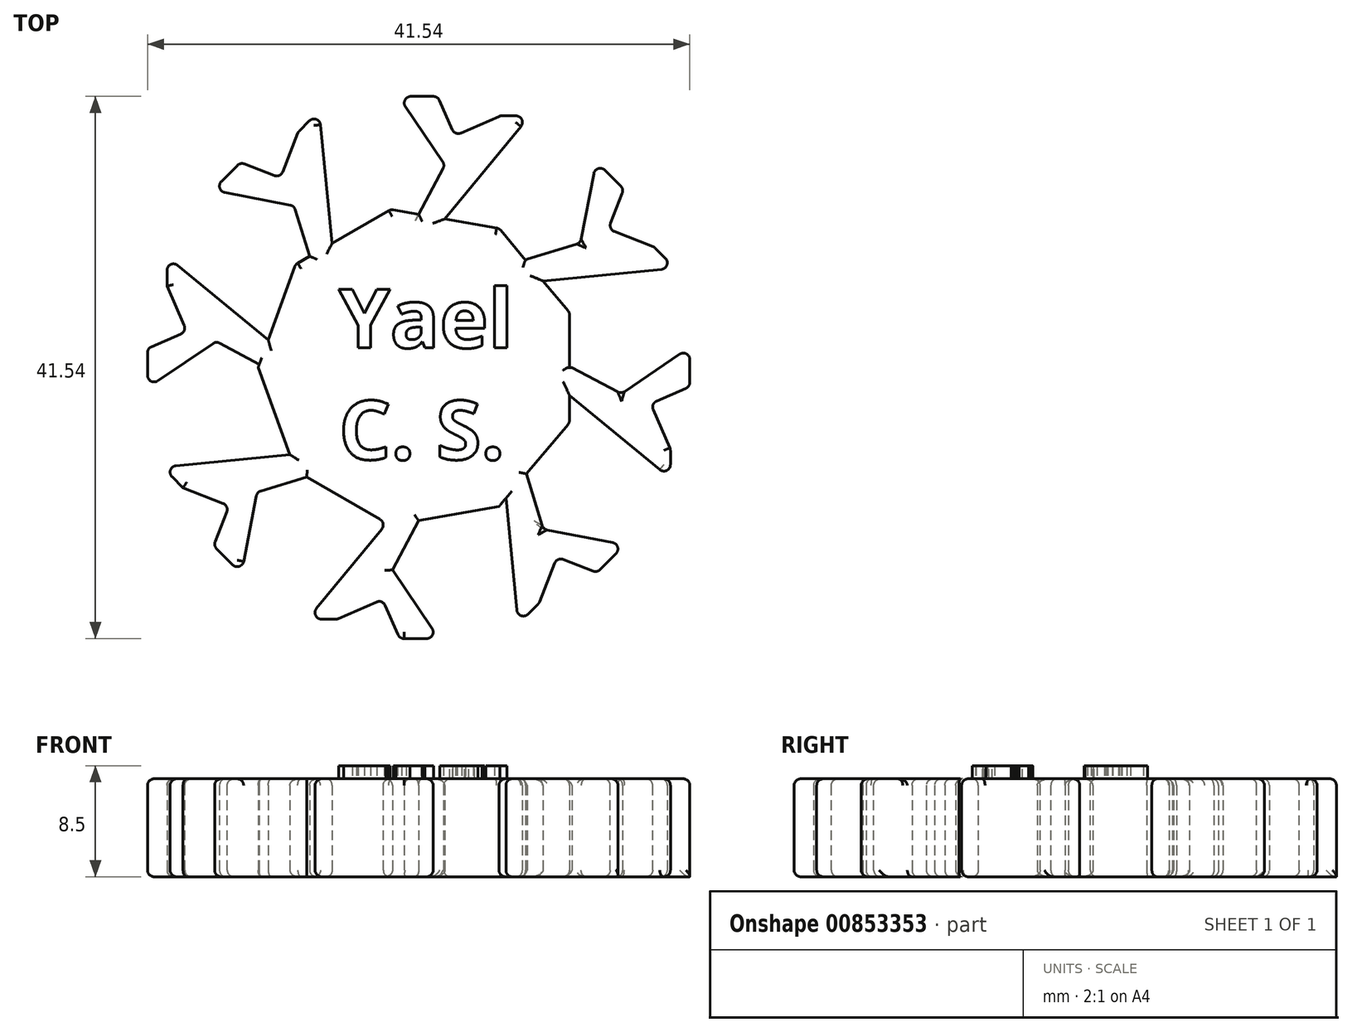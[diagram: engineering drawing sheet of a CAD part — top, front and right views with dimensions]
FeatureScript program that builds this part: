
annotation { "Feature Type Name" : "Feature", "Feature Type Description" : "" }
export const myFeature = defineFeature(function(context is Context, id is Id, definition is map)
    precondition{}
    {
        {
            var Q0;
            Q0=qCreatedBy(makeId("Top.planeOp"),FACE);
            var sketch = newSketch(context, id + "F0", { "sketchPlane" : qUnion([Q0])});
            skLineSegment(sketch, "E0.cCircle", {"start": v(11.56, 0) * mm, "end": v(11.56, 0) * mm});
            skLineSegment(sketch, "E0.0", {"start": v(11.56, 4.2) * mm, "end": v(11.56, 0) * mm});
            skLineSegment(sketch, "E0.1", {"start": v(11.56, -4.2) * mm, "end": v(8.25, -8.15) * mm});
            skLineSegment(sketch, "E0.2", {"start": v(6.15, -10.65) * mm, "end": v(0, -11.74) * mm});
            skLineSegment(sketch, "E0.3", {"start": v(-2.46, -11.93) * mm, "end": v(-8.6, -8.39) * mm});
            skLineSegment(sketch, "E0.4", {"start": v(-9.87, -6.67) * mm, "end": v(-12.3, 0) * mm});
            skLineSegment(sketch, "E0.5", {"start": v(-12.3, 0) * mm, "end": v(-12.21, 0.25) * mm});
            skLineSegment(sketch, "E0.6", {"start": v(-9.42, 7.9) * mm, "end": v(-8.37, 8.52) * mm});
            skLineSegment(sketch, "E0.7", {"start": v(-2.14, 12.12) * mm, "end": v(0, 11.74) * mm});
            skLineSegment(sketch, "E0.8", {"start": v(6.15, 10.65) * mm, "end": v(8.2, 8.21) * mm});
            skPoint(sketch, "E0.0.midPoint", {"position": v(11.56, 0) * mm});
            skLineSegment(sketch, "E1", {"start": v(-1.55, 20.77) * mm, "end": v(1.46, 20.77) * mm});
            skLineSegment(sketch, "E2", {"start": v(1.46, 20.77) * mm, "end": v(2.77, 17.77) * mm});
            skLineSegment(sketch, "E3", {"start": v(2.77, 17.77) * mm, "end": v(6.25, 19.29) * mm});
            skLineSegment(sketch, "E4", {"start": v(6.25, 19.29) * mm, "end": v(8.5, 19.29) * mm});
            skLineSegment(sketch, "E5", {"start": v(8.5, 19.29) * mm, "end": v(2, 11.38) * mm});
            skLineSegment(sketch, "E6", {"start": v(0, 11.74) * mm, "end": v(2, 15.51) * mm});
            skLineSegment(sketch, "E7", {"start": v(2, 15.51) * mm, "end": v(-1.55, 20.77) * mm});
            skLineSegment(sketch, "E8.1.0", {"start": v(-9.55, 12.39) * mm, "end": v(-15.78, 13.6) * mm});
            skLineSegment(sketch, "E8.1.1", {"start": v(-15.78, 13.6) * mm, "end": v(-13.66, 15.72) * mm});
            skLineSegment(sketch, "E8.1.2", {"start": v(-13.66, 15.72) * mm, "end": v(-10.6, 14.52) * mm});
            skLineSegment(sketch, "E8.1.3", {"start": v(-10.6, 14.52) * mm, "end": v(-9.22, 18.05) * mm});
            skLineSegment(sketch, "E8.1.4", {"start": v(-9.22, 18.05) * mm, "end": v(-7.63, 19.65) * mm});
            skLineSegment(sketch, "E8.1.5", {"start": v(-7.63, 19.65) * mm, "end": v(-6.63, 9.47) * mm});
            skLineSegment(sketch, "E8.1.6", {"start": v(-8.37, 8.52) * mm, "end": v(-9.55, 12.39) * mm});
            skLineSegment(sketch, "E8.2.0", {"start": v(-15.51, 2) * mm, "end": v(-20.77, -1.55) * mm});
            skLineSegment(sketch, "E8.2.1", {"start": v(-20.77, -1.55) * mm, "end": v(-20.77, 1.46) * mm});
            skLineSegment(sketch, "E8.2.2", {"start": v(-20.77, 1.46) * mm, "end": v(-17.77, 2.77) * mm});
            skLineSegment(sketch, "E8.2.3", {"start": v(-17.77, 2.77) * mm, "end": v(-19.29, 6.25) * mm});
            skLineSegment(sketch, "E8.2.4", {"start": v(-19.29, 6.25) * mm, "end": v(-19.29, 8.5) * mm});
            skLineSegment(sketch, "E8.2.5", {"start": v(-19.29, 8.5) * mm, "end": v(-11.38, 2) * mm});
            skLineSegment(sketch, "E8.2.6", {"start": v(-12.21, 0.25) * mm, "end": v(-15.51, 2) * mm});
            skLineSegment(sketch, "E8.3.0", {"start": v(-12.39, -9.55) * mm, "end": v(-13.6, -15.78) * mm});
            skLineSegment(sketch, "E8.3.1", {"start": v(-13.6, -15.78) * mm, "end": v(-15.72, -13.66) * mm});
            skLineSegment(sketch, "E8.3.2", {"start": v(-15.72, -13.66) * mm, "end": v(-14.52, -10.6) * mm});
            skLineSegment(sketch, "E8.3.3", {"start": v(-14.52, -10.6) * mm, "end": v(-18.05, -9.22) * mm});
            skLineSegment(sketch, "E8.3.4", {"start": v(-18.05, -9.22) * mm, "end": v(-19.65, -7.63) * mm});
            skLineSegment(sketch, "E8.3.5", {"start": v(-19.65, -7.63) * mm, "end": v(-9.47, -6.63) * mm});
            skLineSegment(sketch, "E8.3.6", {"start": v(-8.3, -8.3) * mm, "end": v(-12.39, -9.55) * mm});
            skLineSegment(sketch, "E8.4.0", {"start": v(-2, -15.51) * mm, "end": v(1.55, -20.77) * mm});
            skLineSegment(sketch, "E8.4.1", {"start": v(1.55, -20.77) * mm, "end": v(-1.46, -20.77) * mm});
            skLineSegment(sketch, "E8.4.2", {"start": v(-1.46, -20.77) * mm, "end": v(-2.77, -17.77) * mm});
            skLineSegment(sketch, "E8.4.3", {"start": v(-2.77, -17.77) * mm, "end": v(-6.25, -19.29) * mm});
            skLineSegment(sketch, "E8.4.4", {"start": v(-6.25, -19.29) * mm, "end": v(-8.5, -19.29) * mm});
            skLineSegment(sketch, "E8.4.5", {"start": v(-8.5, -19.29) * mm, "end": v(-2.46, -11.93) * mm});
            skLineSegment(sketch, "E8.4.6", {"start": v(0, -11.74) * mm, "end": v(-2, -15.51) * mm});
            skLineSegment(sketch, "E8.5.0", {"start": v(9.55, -12.39) * mm, "end": v(15.78, -13.6) * mm});
            skLineSegment(sketch, "E8.5.1", {"start": v(15.78, -13.6) * mm, "end": v(13.66, -15.72) * mm});
            skLineSegment(sketch, "E8.5.2", {"start": v(13.66, -15.72) * mm, "end": v(10.6, -14.52) * mm});
            skLineSegment(sketch, "E8.5.3", {"start": v(10.6, -14.52) * mm, "end": v(9.22, -18.05) * mm});
            skLineSegment(sketch, "E8.5.4", {"start": v(9.22, -18.05) * mm, "end": v(7.63, -19.65) * mm});
            skLineSegment(sketch, "E8.5.5", {"start": v(7.63, -19.65) * mm, "end": v(6.68, -10.02) * mm});
            skLineSegment(sketch, "E8.5.6", {"start": v(8.3, -8.3) * mm, "end": v(9.55, -12.39) * mm});
            skLineSegment(sketch, "E8.6.0", {"start": v(15.51, -2) * mm, "end": v(20.77, 1.55) * mm});
            skLineSegment(sketch, "E8.6.1", {"start": v(20.77, 1.55) * mm, "end": v(20.77, -1.46) * mm});
            skLineSegment(sketch, "E8.6.2", {"start": v(20.77, -1.46) * mm, "end": v(17.77, -2.77) * mm});
            skLineSegment(sketch, "E8.6.3", {"start": v(17.77, -2.77) * mm, "end": v(19.29, -6.25) * mm});
            skLineSegment(sketch, "E8.6.4", {"start": v(19.29, -6.25) * mm, "end": v(19.29, -8.5) * mm});
            skLineSegment(sketch, "E8.6.5", {"start": v(19.29, -8.5) * mm, "end": v(11.38, -2) * mm});
            skLineSegment(sketch, "E8.6.6", {"start": v(11.74, 0) * mm, "end": v(15.51, -2) * mm});
            skLineSegment(sketch, "E8.7.0", {"start": v(12.39, 9.55) * mm, "end": v(13.6, 15.78) * mm});
            skLineSegment(sketch, "E8.7.1", {"start": v(13.6, 15.78) * mm, "end": v(15.72, 13.66) * mm});
            skLineSegment(sketch, "E8.7.2", {"start": v(15.72, 13.66) * mm, "end": v(14.52, 10.6) * mm});
            skLineSegment(sketch, "E8.7.3", {"start": v(14.52, 10.6) * mm, "end": v(18.05, 9.22) * mm});
            skLineSegment(sketch, "E8.7.4", {"start": v(18.05, 9.22) * mm, "end": v(19.65, 7.63) * mm});
            skLineSegment(sketch, "E8.7.5", {"start": v(19.65, 7.63) * mm, "end": v(9.47, 6.63) * mm});
            skLineSegment(sketch, "E8.7.6", {"start": v(8.3, 8.3) * mm, "end": v(12.39, 9.55) * mm});
            skLineSegment(sketch, "E9", {"start": v(8.3, 8.3) * mm, "end": v(8.2, 8.21) * mm});
            skLineSegment(sketch, "E10", {"start": v(11.74, 0) * mm, "end": v(11.56, 0) * mm});
            skLineSegment(sketch, "E11", {"start": v(8.3, -8.3) * mm, "end": v(8.25, -8.15) * mm});
            skPoint(sketch, "E12.orphan", {"position": v(-2.14, -12.12) * mm});
            skLineSegment(sketch, "E13.trimOffspring", {"start": v(6.68, -10.02) * mm, "end": v(6.15, -10.65) * mm});
            skPoint(sketch, "E14.orphan", {"position": v(-9.42, -7.9) * mm});
            skLineSegment(sketch, "E15.trimOffspring", {"start": v(11.56, -2.15) * mm, "end": v(11.56, -4.2) * mm});
            skArc(sketch, "E16.trimOffspring", {"start": v(-5.78, 10.01) * mm, "mid": v(-6.21, 9.75) * mm, "end": v(-6.63, 9.47) * mm, "construction": true});
            skPoint(sketch, "E17.orphan", {"position": v(-2, -11.38) * mm});
            skPoint(sketch, "E18.orphan", {"position": v(6.63, -9.47) * mm});
            skLineSegment(sketch, "E19.trimOffspring", {"start": v(-11.53, 2.13) * mm, "end": v(-9.42, 7.9) * mm});
            skPoint(sketch, "E20.orphan", {"position": v(-11.74, 0) * mm});
            skPoint(sketch, "E21.orphan", {"position": v(-8.3, 8.3) * mm});
            skLineSegment(sketch, "E22.trimOffspring", {"start": v(9.52, 6.64) * mm, "end": v(11.56, 4.2) * mm});
            skLineSegment(sketch, "E23.trimOffspring", {"start": v(2, 11.38) * mm, "end": v(6.15, 10.65) * mm});
            skLineSegment(sketch, "E24.trimOffspring", {"start": v(-6.64, 9.52) * mm, "end": v(-2.14, 12.12) * mm});
            skSolve(sketch);
        }
        {
            var Q0;
            Q0=makeQuery(id+"F0.imprint","IMPRINT",FACE,{"disambiguationData":[TD([[makeQuery(id+"F0.imprint","IMPRINT",EDGE,{"derivedFrom":sQuery(id+"F0.wireOp",EDGE,"E0.0")}),-1.0]])]});
            extrude(context, id + "F1", {"entities" : qUnion([Q0]), "depth" : 7.5 * mm, "offsetDistance" : 25 * mm});
        }
        {
            var Q0;
            Q0=makeQuery(id+"F1.opExtrude","CAP_EDGE",EDGE,{"disambiguationData":[OSD([sQuery(id+"F0.wireOp",EDGE,"E8.1.2")])],"isStart":false});
            var Q1;
            Q1=makeQuery(id+"F1.opExtrude","CAP_EDGE",EDGE,{"disambiguationData":[OSD([sQuery(id+"F0.wireOp",EDGE,"E8.1.1")])],"isStart":false});
            var Q2;
            Q2=makeQuery(id+"F1.opExtrude","CAP_EDGE",EDGE,{"disambiguationData":[OSD([sQuery(id+"F0.wireOp",EDGE,"E8.1.0")])],"isStart":false});
            var Q3;
            Q3=makeQuery(id+"F1.opExtrude","CAP_EDGE",EDGE,{"disambiguationData":[OSD([sQuery(id+"F0.wireOp",EDGE,"E8.1.3")])],"isStart":false});
            var Q4;
            Q4=makeQuery(id+"F1.opExtrude","CAP_EDGE",EDGE,{"disambiguationData":[OSD([sQuery(id+"F0.wireOp",EDGE,"E8.1.6")])],"isStart":false});
            var Q5;
            Q5=makeQuery(id+"F1.opExtrude","CAP_EDGE",EDGE,{"disambiguationData":[OSD([sQuery(id+"F0.wireOp",EDGE,"E24.trimOffspring")])],"isStart":false});
            var Q6;
            Q6=makeQuery(id+"F1.opExtrude","CAP_EDGE",EDGE,{"disambiguationData":[OSD([sQuery(id+"F0.wireOp",EDGE,"E0.6")])],"isStart":false});
            var Q7;
            Q7=makeQuery(id+"F1.opExtrude","CAP_EDGE",EDGE,{"disambiguationData":[OSD([sQuery(id+"F0.wireOp",EDGE,"E0.6")])],"isStart":true});
            var Q8;
            Q8=makeQuery(id+"F1.opExtrude","CAP_EDGE",EDGE,{"disambiguationData":[OSD([sQuery(id+"F0.wireOp",EDGE,"E8.1.6")])],"isStart":true});
            var Q9;
            Q9=makeQuery(id+"F1.opExtrude","SWEPT_EDGE",EDGE,{"disambiguationData":[OSD([sQuery(id+"F0.wireOp",EDGE,"E8.1.0"),sQuery(id+"F0.wireOp",EDGE,"E8.1.1")])]});
            var Q10;
            Q10=makeQuery(id+"F1.opExtrude","CAP_EDGE",EDGE,{"disambiguationData":[OSD([sQuery(id+"F0.wireOp",EDGE,"E8.1.1")])],"isStart":true});
            var Q11;
            Q11=makeQuery(id+"F1.opExtrude","SWEPT_EDGE",EDGE,{"disambiguationData":[OSD([sQuery(id+"F0.wireOp",EDGE,"E8.1.1"),sQuery(id+"F0.wireOp",EDGE,"E8.1.2")])]});
            var Q12;
            Q12=makeQuery(id+"F1.opExtrude","SWEPT_EDGE",EDGE,{"disambiguationData":[OSD([sQuery(id+"F0.wireOp",EDGE,"E8.1.3"),sQuery(id+"F0.wireOp",EDGE,"E8.1.4")])]});
            var Q13;
            Q13=makeQuery(id+"F1.opExtrude","CAP_EDGE",EDGE,{"disambiguationData":[OSD([sQuery(id+"F0.wireOp",EDGE,"E8.1.3")])],"isStart":true});
            var Q14;
            Q14=makeQuery(id+"F1.opExtrude","SWEPT_EDGE",EDGE,{"disambiguationData":[OSD([sQuery(id+"F0.wireOp",EDGE,"E1"),sQuery(id+"F0.wireOp",EDGE,"E7")])]});
            var Q15;
            Q15=makeQuery(id+"F1.opExtrude","CAP_EDGE",EDGE,{"disambiguationData":[OSD([sQuery(id+"F0.wireOp",EDGE,"E8.1.4")])],"isStart":false});
            var Q16;
            Q16=makeQuery(id+"F1.opExtrude","CAP_EDGE",EDGE,{"disambiguationData":[OSD([sQuery(id+"F0.wireOp",EDGE,"E8.1.5")])],"isStart":false});
            var Q17;
            Q17=makeQuery(id+"F1.opExtrude","CAP_EDGE",EDGE,{"disambiguationData":[OSD([sQuery(id+"F0.wireOp",EDGE,"E1")])],"isStart":false});
            var Q18;
            Q18=makeQuery(id+"F1.opExtrude","CAP_EDGE",EDGE,{"disambiguationData":[OSD([sQuery(id+"F0.wireOp",EDGE,"E7")])],"isStart":false});
            var Q19;
            Q19=makeQuery(id+"F1.opExtrude","CAP_EDGE",EDGE,{"disambiguationData":[OSD([sQuery(id+"F0.wireOp",EDGE,"E2")])],"isStart":false});
            var Q20;
            Q20=makeQuery(id+"F1.opExtrude","CAP_EDGE",EDGE,{"disambiguationData":[OSD([sQuery(id+"F0.wireOp",EDGE,"E3")])],"isStart":false});
            var Q21;
            Q21=makeQuery(id+"F1.opExtrude","CAP_EDGE",EDGE,{"disambiguationData":[OSD([sQuery(id+"F0.wireOp",EDGE,"E5")])],"isStart":false});
            var Q22;
            Q22=makeQuery(id+"F1.opExtrude","CAP_EDGE",EDGE,{"disambiguationData":[OSD([sQuery(id+"F0.wireOp",EDGE,"E4")])],"isStart":false});
            var Q23;
            Q23=makeQuery(id+"F1.opExtrude","CAP_EDGE",EDGE,{"disambiguationData":[OSD([sQuery(id+"F0.wireOp",EDGE,"E6")])],"isStart":false});
            var Q24;
            Q24=makeQuery(id+"F1.opExtrude","CAP_EDGE",EDGE,{"disambiguationData":[OSD([sQuery(id+"F0.wireOp",EDGE,"E8.1.4")])],"isStart":true});
            var Q25;
            Q25=makeQuery(id+"F1.opExtrude","CAP_EDGE",EDGE,{"disambiguationData":[OSD([sQuery(id+"F0.wireOp",EDGE,"E8.1.5")])],"isStart":true});
            var Q26;
            Q26=makeQuery(id+"F1.opExtrude","CAP_EDGE",EDGE,{"disambiguationData":[OSD([sQuery(id+"F0.wireOp",EDGE,"E8.1.0")])],"isStart":true});
            var Q27;
            Q27=makeQuery(id+"F1.opExtrude","CAP_EDGE",EDGE,{"disambiguationData":[OSD([sQuery(id+"F0.wireOp",EDGE,"E7")])],"isStart":true});
            var Q28;
            Q28=makeQuery(id+"F1.opExtrude","CAP_EDGE",EDGE,{"disambiguationData":[OSD([sQuery(id+"F0.wireOp",EDGE,"E2")])],"isStart":true});
            var Q29;
            Q29=makeQuery(id+"F1.opExtrude","CAP_EDGE",EDGE,{"disambiguationData":[OSD([sQuery(id+"F0.wireOp",EDGE,"E3")])],"isStart":true});
            var Q30;
            Q30=makeQuery(id+"F1.opExtrude","CAP_EDGE",EDGE,{"disambiguationData":[OSD([sQuery(id+"F0.wireOp",EDGE,"E4")])],"isStart":true});
            var Q31;
            Q31=makeQuery(id+"F1.opExtrude","CAP_EDGE",EDGE,{"disambiguationData":[OSD([sQuery(id+"F0.wireOp",EDGE,"E5")])],"isStart":true});
            var Q32;
            Q32=makeQuery(id+"F1.opExtrude","SWEPT_EDGE",EDGE,{"disambiguationData":[OSD([sQuery(id+"F0.wireOp",EDGE,"E1"),sQuery(id+"F0.wireOp",EDGE,"E2")])]});
            var Q33;
            Q33=makeQuery(id+"F1.opExtrude","SWEPT_EDGE",EDGE,{"disambiguationData":[OSD([sQuery(id+"F0.wireOp",EDGE,"E3"),sQuery(id+"F0.wireOp",EDGE,"E4")])]});
            var Q34;
            Q34=makeQuery(id+"F1.opExtrude","SWEPT_FACE",FACE,{"disambiguationData":[OSD([sQuery(id+"F0.wireOp",EDGE,"E8.1.2")])]});
            var Q35;
            Q35=makeQuery(id+"F1.opExtrude","CAP_EDGE",EDGE,{"disambiguationData":[OSD([sQuery(id+"F0.wireOp",EDGE,"E8.2.5")])],"isStart":true});
            var Q36;
            Q36=makeQuery(id+"F1.opExtrude","CAP_EDGE",EDGE,{"disambiguationData":[OSD([sQuery(id+"F0.wireOp",EDGE,"E8.2.4")])],"isStart":true});
            var Q37;
            Q37=makeQuery(id+"F1.opExtrude","CAP_EDGE",EDGE,{"disambiguationData":[OSD([sQuery(id+"F0.wireOp",EDGE,"E8.2.3")])],"isStart":true});
            var Q38;
            Q38=makeQuery(id+"F1.opExtrude","CAP_EDGE",EDGE,{"disambiguationData":[OSD([sQuery(id+"F0.wireOp",EDGE,"E8.2.2")])],"isStart":true});
            var Q39;
            Q39=makeQuery(id+"F1.opExtrude","CAP_EDGE",EDGE,{"disambiguationData":[OSD([sQuery(id+"F0.wireOp",EDGE,"E8.2.1")])],"isStart":true});
            var Q40;
            Q40=makeQuery(id+"F1.opExtrude","CAP_EDGE",EDGE,{"disambiguationData":[OSD([sQuery(id+"F0.wireOp",EDGE,"E8.2.0")])],"isStart":true});
            var Q41;
            Q41=makeQuery(id+"F1.opExtrude","CAP_EDGE",EDGE,{"disambiguationData":[OSD([sQuery(id+"F0.wireOp",EDGE,"E8.2.6")])],"isStart":true});
            var Q42;
            Q42=makeQuery(id+"F1.opExtrude","SWEPT_EDGE",EDGE,{"disambiguationData":[OSD([sQuery(id+"F0.wireOp",EDGE,"E8.3.4"),sQuery(id+"F0.wireOp",EDGE,"E8.3.5")])]});
            var Q43;
            Q43=makeQuery(id+"F1.opExtrude","SWEPT_EDGE",EDGE,{"disambiguationData":[OSD([sQuery(id+"F0.wireOp",EDGE,"E8.2.4"),sQuery(id+"F0.wireOp",EDGE,"E8.2.5")])]});
            var Q44;
            Q44=makeQuery(id+"F1.opExtrude","SWEPT_EDGE",EDGE,{"disambiguationData":[OSD([sQuery(id+"F0.wireOp",EDGE,"E8.2.1"),sQuery(id+"F0.wireOp",EDGE,"E8.2.2")])]});
            var Q45;
            Q45=makeQuery(id+"F1.opExtrude","CAP_EDGE",EDGE,{"disambiguationData":[OSD([sQuery(id+"F0.wireOp",EDGE,"E8.3.5")])],"isStart":true});
            var Q46;
            Q46=makeQuery(id+"F1.opExtrude","CAP_EDGE",EDGE,{"disambiguationData":[OSD([sQuery(id+"F0.wireOp",EDGE,"E8.3.3")])],"isStart":true});
            var Q47;
            Q47=makeQuery(id+"F1.opExtrude","CAP_EDGE",EDGE,{"disambiguationData":[OSD([sQuery(id+"F0.wireOp",EDGE,"E8.3.4")])],"isStart":true});
            var Q48;
            Q48=makeQuery(id+"F1.opExtrude","CAP_EDGE",EDGE,{"disambiguationData":[OSD([sQuery(id+"F0.wireOp",EDGE,"E8.3.2")])],"isStart":true});
            var Q49;
            Q49=makeQuery(id+"F1.opExtrude","CAP_EDGE",EDGE,{"disambiguationData":[OSD([sQuery(id+"F0.wireOp",EDGE,"E8.3.1")])],"isStart":true});
            var Q50;
            Q50=makeQuery(id+"F1.opExtrude","CAP_EDGE",EDGE,{"disambiguationData":[OSD([sQuery(id+"F0.wireOp",EDGE,"E8.3.0")])],"isStart":true});
            var Q51;
            Q51=makeQuery(id+"F1.opExtrude","CAP_EDGE",EDGE,{"disambiguationData":[OSD([sQuery(id+"F0.wireOp",EDGE,"E8.3.6")])],"isStart":true});
            var Q52;
            Q52=makeQuery(id+"F1.opExtrude","CAP_EDGE",EDGE,{"disambiguationData":[OSD([sQuery(id+"F0.wireOp",EDGE,"E8.2.3")])],"isStart":false});
            var Q53;
            Q53=makeQuery(id+"F1.opExtrude","CAP_EDGE",EDGE,{"disambiguationData":[OSD([sQuery(id+"F0.wireOp",EDGE,"E8.2.5")])],"isStart":false});
            var Q54;
            Q54=makeQuery(id+"F1.opExtrude","CAP_EDGE",EDGE,{"disambiguationData":[OSD([sQuery(id+"F0.wireOp",EDGE,"E8.2.4")])],"isStart":false});
            var Q55;
            Q55=makeQuery(id+"F1.opExtrude","CAP_EDGE",EDGE,{"disambiguationData":[OSD([sQuery(id+"F0.wireOp",EDGE,"E8.2.2")])],"isStart":false});
            var Q56;
            Q56=makeQuery(id+"F1.opExtrude","CAP_EDGE",EDGE,{"disambiguationData":[OSD([sQuery(id+"F0.wireOp",EDGE,"E8.2.1")])],"isStart":false});
            var Q57;
            Q57=makeQuery(id+"F1.opExtrude","CAP_EDGE",EDGE,{"disambiguationData":[OSD([sQuery(id+"F0.wireOp",EDGE,"E8.2.0")])],"isStart":false});
            var Q58;
            Q58=makeQuery(id+"F1.opExtrude","SWEPT_EDGE",EDGE,{"disambiguationData":[OSD([sQuery(id+"F0.wireOp",EDGE,"E8.2.0"),sQuery(id+"F0.wireOp",EDGE,"E8.2.6")])]});
            var Q59;
            Q59=makeQuery(id+"F1.opExtrude","CAP_EDGE",EDGE,{"disambiguationData":[OSD([sQuery(id+"F0.wireOp",EDGE,"E8.2.6")])],"isStart":false});
            var Q60;
            Q60=makeQuery(id+"F1.opExtrude","SWEPT_EDGE",EDGE,{"disambiguationData":[OSD([sQuery(id+"F0.wireOp",EDGE,"E8.1.0"),sQuery(id+"F0.wireOp",EDGE,"E8.1.6")])]});
            var Q61;
            Q61=makeQuery(id+"F1.opExtrude","SWEPT_EDGE",EDGE,{"disambiguationData":[OSD([sQuery(id+"F0.wireOp",EDGE,"E6"),sQuery(id+"F0.wireOp",EDGE,"E7")])]});
            var Q62;
            Q62=makeQuery(id+"F1.opExtrude","SWEPT_EDGE",EDGE,{"disambiguationData":[OSD([sQuery(id+"F0.wireOp",EDGE,"E8.3.1"),sQuery(id+"F0.wireOp",EDGE,"E8.3.2")])]});
            var Q63;
            Q63=makeQuery(id+"F1.opExtrude","SWEPT_EDGE",EDGE,{"disambiguationData":[OSD([sQuery(id+"F0.wireOp",EDGE,"E8.3.0"),sQuery(id+"F0.wireOp",EDGE,"E8.3.6")])]});
            var Q64;
            Q64=makeQuery(id+"F1.opExtrude","CAP_EDGE",EDGE,{"disambiguationData":[OSD([sQuery(id+"F0.wireOp",EDGE,"E8.3.0")])],"isStart":false});
            var Q65;
            Q65=makeQuery(id+"F1.opExtrude","CAP_EDGE",EDGE,{"disambiguationData":[OSD([sQuery(id+"F0.wireOp",EDGE,"E8.3.6")])],"isStart":false});
            var Q66;
            Q66=makeQuery(id+"F1.opExtrude","SWEPT_EDGE",EDGE,{"disambiguationData":[OSD([sQuery(id+"F0.wireOp",EDGE,"E8.3.2"),sQuery(id+"F0.wireOp",EDGE,"E8.3.3")])]});
            var Q67;
            Q67=makeQuery(id+"F1.opExtrude","SWEPT_EDGE",EDGE,{"disambiguationData":[OSD([sQuery(id+"F0.wireOp",EDGE,"E2"),sQuery(id+"F0.wireOp",EDGE,"E3")])]});
            var Q68;
            Q68=makeQuery(id+"F1.opExtrude","SWEPT_EDGE",EDGE,{"disambiguationData":[OSD([sQuery(id+"F0.wireOp",EDGE,"E8.2.2"),sQuery(id+"F0.wireOp",EDGE,"E8.2.3")])]});
            fillet(context, id + "F2", {"entities" : qUnion([Q0, Q1, Q2, Q3, Q4, Q5, Q6, Q7, Q8, Q9, Q10, Q11, Q12, Q13, Q14, Q15, Q16, Q17, Q18, Q19, Q20, Q21, Q22, Q23, Q24, Q25, Q26, Q27, Q28, Q29, Q30, Q31, Q32, Q33, Q34, Q35, Q36, Q37, Q38, Q39, Q40, Q41, Q42, Q43, Q44, Q45, Q46, Q47, Q48, Q49, Q50, Q51, Q52, Q53, Q54, Q55, Q56, Q57, Q58, Q59, Q60, Q61, Q62, Q63, Q64, Q65, Q66, Q67, Q68]), "radius" : 0.5 * mm, "tangentPropagation" : true, "allowEdgeOverflow" : false});
        }
        {
            var Q0;
            Q0=makeQuery(id+"F1.opExtrude","CAP_EDGE",EDGE,{"disambiguationData":[OSD([sQuery(id+"F0.wireOp",EDGE,"E8.7.0")])],"isStart":false});
            var Q1;
            Q1=makeQuery(id+"F1.opExtrude","CAP_EDGE",EDGE,{"disambiguationData":[OSD([sQuery(id+"F0.wireOp",EDGE,"E8.7.6")])],"isStart":false});
            var Q2;
            Q2=makeQuery(id+"F1.opExtrude","CAP_EDGE",EDGE,{"disambiguationData":[OSD([sQuery(id+"F0.wireOp",EDGE,"E8.7.6")])],"isStart":true});
            var Q3;
            Q3=makeQuery(id+"F1.opExtrude","CAP_EDGE",EDGE,{"disambiguationData":[OSD([sQuery(id+"F0.wireOp",EDGE,"E8.7.1")])],"isStart":false});
            var Q4;
            Q4=makeQuery(id+"F1.opExtrude","CAP_EDGE",EDGE,{"disambiguationData":[OSD([sQuery(id+"F0.wireOp",EDGE,"E8.7.1")])],"isStart":true});
            var Q5;
            Q5=makeQuery(id+"F1.opExtrude","SWEPT_EDGE",EDGE,{"disambiguationData":[OSD([sQuery(id+"F0.wireOp",EDGE,"E8.7.0"),sQuery(id+"F0.wireOp",EDGE,"E8.7.1")])]});
            var Q6;
            Q6=makeQuery(id+"F1.opExtrude","CAP_EDGE",EDGE,{"disambiguationData":[OSD([sQuery(id+"F0.wireOp",EDGE,"E8.7.2")])],"isStart":false});
            var Q7;
            Q7=makeQuery(id+"F1.opExtrude","SWEPT_EDGE",EDGE,{"disambiguationData":[OSD([sQuery(id+"F0.wireOp",EDGE,"E8.7.1"),sQuery(id+"F0.wireOp",EDGE,"E8.7.2")])]});
            var Q8;
            Q8=makeQuery(id+"F1.opExtrude","CAP_EDGE",EDGE,{"disambiguationData":[OSD([sQuery(id+"F0.wireOp",EDGE,"E8.7.2")])],"isStart":true});
            var Q9;
            Q9=makeQuery(id+"F1.opExtrude","SWEPT_EDGE",EDGE,{"disambiguationData":[OSD([sQuery(id+"F0.wireOp",EDGE,"E8.7.2"),sQuery(id+"F0.wireOp",EDGE,"E8.7.3")])]});
            var Q10;
            Q10=makeQuery(id+"F1.opExtrude","CAP_EDGE",EDGE,{"disambiguationData":[OSD([sQuery(id+"F0.wireOp",EDGE,"E8.7.3")])],"isStart":false});
            var Q11;
            Q11=makeQuery(id+"F1.opExtrude","CAP_EDGE",EDGE,{"disambiguationData":[OSD([sQuery(id+"F0.wireOp",EDGE,"E8.7.3")])],"isStart":true});
            var Q12;
            Q12=makeQuery(id+"F1.opExtrude","SWEPT_EDGE",EDGE,{"disambiguationData":[OSD([sQuery(id+"F0.wireOp",EDGE,"E8.7.3"),sQuery(id+"F0.wireOp",EDGE,"E8.7.4")])]});
            var Q13;
            Q13=makeQuery(id+"F1.opExtrude","CAP_EDGE",EDGE,{"disambiguationData":[OSD([sQuery(id+"F0.wireOp",EDGE,"E8.7.4")])],"isStart":true});
            var Q14;
            Q14=makeQuery(id+"F1.opExtrude","CAP_EDGE",EDGE,{"disambiguationData":[OSD([sQuery(id+"F0.wireOp",EDGE,"E8.7.4")])],"isStart":false});
            var Q15;
            Q15=makeQuery(id+"F1.opExtrude","CAP_EDGE",EDGE,{"disambiguationData":[OSD([sQuery(id+"F0.wireOp",EDGE,"E8.7.5")])],"isStart":false});
            var Q16;
            Q16=makeQuery(id+"F1.opExtrude","CAP_EDGE",EDGE,{"disambiguationData":[OSD([sQuery(id+"F0.wireOp",EDGE,"E8.7.5")])],"isStart":true});
            var Q17;
            Q17=makeQuery(id+"F1.opExtrude","CAP_EDGE",EDGE,{"disambiguationData":[OSD([sQuery(id+"F0.wireOp",EDGE,"E8.7.0")])],"isStart":true});
            var Q18;
            Q18=makeQuery(id+"F1.opExtrude","CAP_EDGE",EDGE,{"disambiguationData":[OSD([sQuery(id+"F0.wireOp",EDGE,"E8.6.0")])],"isStart":false});
            var Q19;
            Q19=makeQuery(id+"F1.opExtrude","CAP_EDGE",EDGE,{"disambiguationData":[OSD([sQuery(id+"F0.wireOp",EDGE,"E8.6.6")])],"isStart":false});
            var Q20;
            Q20=makeQuery(id+"F1.opExtrude","CAP_EDGE",EDGE,{"disambiguationData":[OSD([sQuery(id+"F0.wireOp",EDGE,"E8.6.5")])],"isStart":false});
            var Q21;
            Q21=makeQuery(id+"F1.opExtrude","CAP_EDGE",EDGE,{"disambiguationData":[OSD([sQuery(id+"F0.wireOp",EDGE,"E8.6.1")])],"isStart":false});
            var Q22;
            Q22=makeQuery(id+"F1.opExtrude","CAP_EDGE",EDGE,{"disambiguationData":[OSD([sQuery(id+"F0.wireOp",EDGE,"E8.6.2")])],"isStart":false});
            var Q23;
            Q23=makeQuery(id+"F1.opExtrude","CAP_EDGE",EDGE,{"disambiguationData":[OSD([sQuery(id+"F0.wireOp",EDGE,"E8.6.3")])],"isStart":false});
            var Q24;
            Q24=makeQuery(id+"F1.opExtrude","CAP_EDGE",EDGE,{"disambiguationData":[OSD([sQuery(id+"F0.wireOp",EDGE,"E8.6.4")])],"isStart":false});
            var Q25;
            Q25=makeQuery(id+"F1.opExtrude","SWEPT_EDGE",EDGE,{"disambiguationData":[OSD([sQuery(id+"F0.wireOp",EDGE,"E8.6.3"),sQuery(id+"F0.wireOp",EDGE,"E8.6.4")])]});
            var Q26;
            Q26=makeQuery(id+"F1.opExtrude","SWEPT_EDGE",EDGE,{"disambiguationData":[OSD([sQuery(id+"F0.wireOp",EDGE,"E8.6.2"),sQuery(id+"F0.wireOp",EDGE,"E8.6.3")])]});
            var Q27;
            Q27=makeQuery(id+"F1.opExtrude","SWEPT_EDGE",EDGE,{"disambiguationData":[OSD([sQuery(id+"F0.wireOp",EDGE,"E8.6.1"),sQuery(id+"F0.wireOp",EDGE,"E8.6.2")])]});
            var Q28;
            Q28=makeQuery(id+"F1.opExtrude","SWEPT_EDGE",EDGE,{"disambiguationData":[OSD([sQuery(id+"F0.wireOp",EDGE,"E8.6.0"),sQuery(id+"F0.wireOp",EDGE,"E8.6.1")])]});
            var Q29;
            Q29=makeQuery(id+"F1.opExtrude","CAP_EDGE",EDGE,{"disambiguationData":[OSD([sQuery(id+"F0.wireOp",EDGE,"E8.6.2")])],"isStart":true});
            var Q30;
            Q30=makeQuery(id+"F1.opExtrude","CAP_EDGE",EDGE,{"disambiguationData":[OSD([sQuery(id+"F0.wireOp",EDGE,"E8.6.5")])],"isStart":true});
            var Q31;
            Q31=makeQuery(id+"F1.opExtrude","CAP_EDGE",EDGE,{"disambiguationData":[OSD([sQuery(id+"F0.wireOp",EDGE,"E8.6.3")])],"isStart":true});
            var Q32;
            Q32=makeQuery(id+"F1.opExtrude","CAP_EDGE",EDGE,{"disambiguationData":[OSD([sQuery(id+"F0.wireOp",EDGE,"E8.6.0")])],"isStart":true});
            var Q33;
            Q33=makeQuery(id+"F1.opExtrude","CAP_EDGE",EDGE,{"disambiguationData":[OSD([sQuery(id+"F0.wireOp",EDGE,"E8.6.6")])],"isStart":true});
            var Q34;
            Q34=makeQuery(id+"F1.opExtrude","CAP_EDGE",EDGE,{"disambiguationData":[OSD([sQuery(id+"F0.wireOp",EDGE,"E8.5.6"),sQuery(id+"F0.wireOp",EDGE,"E11")])],"isStart":false});
            var Q35;
            Q35=makeQuery(id+"F1.opExtrude","CAP_EDGE",EDGE,{"disambiguationData":[OSD([sQuery(id+"F0.wireOp",EDGE,"E8.5.5")])],"isStart":false});
            var Q36;
            Q36=makeQuery(id+"F1.opExtrude","CAP_EDGE",EDGE,{"disambiguationData":[OSD([sQuery(id+"F0.wireOp",EDGE,"E8.5.3")])],"isStart":false});
            var Q37;
            Q37=makeQuery(id+"F1.opExtrude","CAP_EDGE",EDGE,{"disambiguationData":[OSD([sQuery(id+"F0.wireOp",EDGE,"E8.5.2")])],"isStart":false});
            var Q38;
            Q38=makeQuery(id+"F1.opExtrude","CAP_EDGE",EDGE,{"disambiguationData":[OSD([sQuery(id+"F0.wireOp",EDGE,"E8.5.0")])],"isStart":false});
            var Q39;
            Q39=makeQuery(id+"F1.opExtrude","CAP_EDGE",EDGE,{"disambiguationData":[OSD([sQuery(id+"F0.wireOp",EDGE,"E8.5.1")])],"isStart":false});
            var Q40;
            Q40=makeQuery(id+"F1.opExtrude","CAP_EDGE",EDGE,{"disambiguationData":[OSD([sQuery(id+"F0.wireOp",EDGE,"E8.5.4")])],"isStart":false});
            var Q41;
            Q41=makeQuery(id+"F1.opExtrude","CAP_EDGE",EDGE,{"disambiguationData":[OSD([sQuery(id+"F0.wireOp",EDGE,"E8.5.1")])],"isStart":true});
            var Q42;
            Q42=makeQuery(id+"F1.opExtrude","SWEPT_EDGE",EDGE,{"disambiguationData":[OSD([sQuery(id+"F0.wireOp",EDGE,"E8.5.0"),sQuery(id+"F0.wireOp",EDGE,"E8.5.1")])]});
            var Q43;
            Q43=makeQuery(id+"F1.opExtrude","SWEPT_EDGE",EDGE,{"disambiguationData":[OSD([sQuery(id+"F0.wireOp",EDGE,"E8.5.1"),sQuery(id+"F0.wireOp",EDGE,"E8.5.2")])]});
            var Q44;
            Q44=makeQuery(id+"F1.opExtrude","SWEPT_EDGE",EDGE,{"disambiguationData":[OSD([sQuery(id+"F0.wireOp",EDGE,"E8.5.2"),sQuery(id+"F0.wireOp",EDGE,"E8.5.3")])]});
            var Q45;
            Q45=makeQuery(id+"F1.opExtrude","SWEPT_EDGE",EDGE,{"disambiguationData":[OSD([sQuery(id+"F0.wireOp",EDGE,"E8.5.3"),sQuery(id+"F0.wireOp",EDGE,"E8.5.4")])]});
            var Q46;
            Q46=makeQuery(id+"F1.opExtrude","CAP_EDGE",EDGE,{"disambiguationData":[OSD([sQuery(id+"F0.wireOp",EDGE,"E8.5.5")])],"isStart":true});
            var Q47;
            Q47=makeQuery(id+"F1.opExtrude","CAP_EDGE",EDGE,{"disambiguationData":[OSD([sQuery(id+"F0.wireOp",EDGE,"E8.5.3")])],"isStart":true});
            var Q48;
            Q48=makeQuery(id+"F1.opExtrude","CAP_EDGE",EDGE,{"disambiguationData":[OSD([sQuery(id+"F0.wireOp",EDGE,"E8.5.4")])],"isStart":true});
            var Q49;
            Q49=makeQuery(id+"F1.opExtrude","CAP_EDGE",EDGE,{"disambiguationData":[OSD([sQuery(id+"F0.wireOp",EDGE,"E8.5.2")])],"isStart":true});
            var Q50;
            Q50=makeQuery(id+"F1.opExtrude","CAP_EDGE",EDGE,{"disambiguationData":[OSD([sQuery(id+"F0.wireOp",EDGE,"E8.5.6"),sQuery(id+"F0.wireOp",EDGE,"E11")])],"isStart":true});
            fillet(context, id + "F3", {"entities" : qUnion([Q0, Q1, Q2, Q3, Q4, Q5, Q6, Q7, Q8, Q9, Q10, Q11, Q12, Q13, Q14, Q15, Q16, Q17, Q18, Q19, Q20, Q21, Q22, Q23, Q24, Q25, Q26, Q27, Q28, Q29, Q30, Q31, Q32, Q33, Q34, Q35, Q36, Q37, Q38, Q39, Q40, Q41, Q42, Q43, Q44, Q45, Q46, Q47, Q48, Q49, Q50]), "radius" : 0.5 * mm, "tangentPropagation" : true, "allowEdgeOverflow" : false});
        }
        {
            var Q0;
            Q0=makeQuery(id+"F1.opExtrude","CAP_EDGE",EDGE,{"disambiguationData":[OSD([sQuery(id+"F0.wireOp",EDGE,"E8.3.4")])],"isStart":false});
            var Q1;
            Q1=makeQuery(id+"F1.opExtrude","CAP_EDGE",EDGE,{"disambiguationData":[OSD([sQuery(id+"F0.wireOp",EDGE,"E8.4.5")])],"isStart":false});
            var Q2;
            Q2=makeQuery(id+"F1.opExtrude","CAP_EDGE",EDGE,{"disambiguationData":[OSD([sQuery(id+"F0.wireOp",EDGE,"E8.4.4")])],"isStart":false});
            var Q3;
            Q3=makeQuery(id+"F1.opExtrude","SWEPT_EDGE",EDGE,{"disambiguationData":[OSD([sQuery(id+"F0.wireOp",EDGE,"E8.4.3"),sQuery(id+"F0.wireOp",EDGE,"E8.4.4")])]});
            var Q4;
            Q4=makeQuery(id+"F1.opExtrude","CAP_EDGE",EDGE,{"disambiguationData":[OSD([sQuery(id+"F0.wireOp",EDGE,"E8.4.3")])],"isStart":false});
            var Q5;
            Q5=makeQuery(id+"F1.opExtrude","CAP_EDGE",EDGE,{"disambiguationData":[OSD([sQuery(id+"F0.wireOp",EDGE,"E8.4.5")])],"isStart":true});
            var Q6;
            Q6=makeQuery(id+"F1.opExtrude","CAP_EDGE",EDGE,{"disambiguationData":[OSD([sQuery(id+"F0.wireOp",EDGE,"E8.4.3")])],"isStart":true});
            var Q7;
            Q7=makeQuery(id+"F1.opExtrude","SWEPT_EDGE",EDGE,{"disambiguationData":[OSD([sQuery(id+"F0.wireOp",EDGE,"E8.4.2"),sQuery(id+"F0.wireOp",EDGE,"E8.4.3")])]});
            var Q8;
            Q8=makeQuery(id+"F1.opExtrude","CAP_EDGE",EDGE,{"disambiguationData":[OSD([sQuery(id+"F0.wireOp",EDGE,"E8.4.2")])],"isStart":true});
            var Q9;
            Q9=makeQuery(id+"F1.opExtrude","CAP_EDGE",EDGE,{"disambiguationData":[OSD([sQuery(id+"F0.wireOp",EDGE,"E8.4.4")])],"isStart":true});
            var Q10;
            Q10=makeQuery(id+"F1.opExtrude","CAP_EDGE",EDGE,{"disambiguationData":[OSD([sQuery(id+"F0.wireOp",EDGE,"E8.3.1")])],"isStart":false});
            var Q11;
            Q11=makeQuery(id+"F1.opExtrude","CAP_EDGE",EDGE,{"disambiguationData":[OSD([sQuery(id+"F0.wireOp",EDGE,"E8.4.1")])],"isStart":false});
            var Q12;
            Q12=makeQuery(id+"F1.opExtrude","CAP_EDGE",EDGE,{"disambiguationData":[OSD([sQuery(id+"F0.wireOp",EDGE,"E8.4.1")])],"isStart":true});
            var Q13;
            Q13=makeQuery(id+"F1.opExtrude","CAP_EDGE",EDGE,{"disambiguationData":[OSD([sQuery(id+"F0.wireOp",EDGE,"E8.4.0")])],"isStart":false});
            var Q14;
            Q14=makeQuery(id+"F1.opExtrude","CAP_EDGE",EDGE,{"disambiguationData":[OSD([sQuery(id+"F0.wireOp",EDGE,"E8.4.6")])],"isStart":false});
            var Q15;
            Q15=makeQuery(id+"F1.opExtrude","CAP_EDGE",EDGE,{"disambiguationData":[OSD([sQuery(id+"F0.wireOp",EDGE,"E8.4.0")])],"isStart":true});
            var Q16;
            Q16=makeQuery(id+"F1.opExtrude","CAP_EDGE",EDGE,{"disambiguationData":[OSD([sQuery(id+"F0.wireOp",EDGE,"E8.4.6")])],"isStart":true});
            var Q17;
            Q17=makeQuery(id+"F1.opExtrude","SWEPT_EDGE",EDGE,{"disambiguationData":[OSD([sQuery(id+"F0.wireOp",EDGE,"E8.4.4"),sQuery(id+"F0.wireOp",EDGE,"E8.4.5")])]});
            var Q18;
            Q18=makeQuery(id+"F1.opExtrude","SWEPT_EDGE",EDGE,{"disambiguationData":[OSD([sQuery(id+"F0.wireOp",EDGE,"E8.4.0"),sQuery(id+"F0.wireOp",EDGE,"E8.4.1")])]});
            var Q19;
            Q19=makeQuery(id+"F1.opExtrude","SWEPT_EDGE",EDGE,{"disambiguationData":[OSD([sQuery(id+"F0.wireOp",EDGE,"E8.2.0"),sQuery(id+"F0.wireOp",EDGE,"E8.2.1")])]});
            var Q20;
            Q20=makeQuery(id+"F1.opExtrude","SWEPT_EDGE",EDGE,{"disambiguationData":[OSD([sQuery(id+"F0.wireOp",EDGE,"E8.1.4"),sQuery(id+"F0.wireOp",EDGE,"E8.1.5")])]});
            var Q21;
            Q21=makeQuery(id+"F1.opExtrude","SWEPT_EDGE",EDGE,{"disambiguationData":[OSD([sQuery(id+"F0.wireOp",EDGE,"E4"),sQuery(id+"F0.wireOp",EDGE,"E5")])]});
            var Q22;
            Q22=makeQuery(id+"F1.opExtrude","SWEPT_EDGE",EDGE,{"disambiguationData":[OSD([sQuery(id+"F0.wireOp",EDGE,"E8.6.4"),sQuery(id+"F0.wireOp",EDGE,"E8.6.5")])]});
            var Q23;
            Q23=makeQuery(id+"F1.opExtrude","SWEPT_EDGE",EDGE,{"disambiguationData":[OSD([sQuery(id+"F0.wireOp",EDGE,"E8.7.4"),sQuery(id+"F0.wireOp",EDGE,"E8.7.5")])]});
            var Q24;
            Q24=makeQuery(id+"F1.opExtrude","SWEPT_EDGE",EDGE,{"disambiguationData":[OSD([sQuery(id+"F0.wireOp",EDGE,"E8.5.4"),sQuery(id+"F0.wireOp",EDGE,"E8.5.5")])]});
            fillet(context, id + "F4", {"entities" : qUnion([Q0, Q1, Q2, Q3, Q4, Q5, Q6, Q7, Q8, Q9, Q10, Q11, Q12, Q13, Q14, Q15, Q16, Q17, Q18, Q19, Q20, Q21, Q22, Q23, Q24]), "radius" : 0.5 * mm, "tangentPropagation" : true, "allowEdgeOverflow" : false});
        }
        {
            var Q0;
            Q0=makeQuery(id+"F1.opExtrude","SWEPT_EDGE",EDGE,{"disambiguationData":[OSD([sQuery(id+"F0.wireOp",EDGE,"E8.6.0"),sQuery(id+"F0.wireOp",EDGE,"E8.6.6")])]});
            var Q1;
            Q1=makeQuery(id+"F1.opExtrude","SWEPT_EDGE",EDGE,{"disambiguationData":[OSD([sQuery(id+"F0.wireOp",EDGE,"E8.7.0"),sQuery(id+"F0.wireOp",EDGE,"E8.7.6")])]});
            var Q2;
            Q2=makeQuery(id+"F1.opExtrude","SWEPT_EDGE",EDGE,{"disambiguationData":[OSD([sQuery(id+"F0.wireOp",EDGE,"E8.5.0"),sQuery(id+"F0.wireOp",EDGE,"E8.5.6")])]});
            fillet(context, id + "F5", {"entities" : qUnion([Q0, Q1, Q2]), "radius" : 0.5 * mm, "tangentPropagation" : true, "allowEdgeOverflow" : false});
        }
        {
            var Q0;
            Q0=makeQuery(id+"F1.opExtrude","SWEPT_EDGE",EDGE,{"disambiguationData":[OSD([sQuery(id+"F0.wireOp",EDGE,"E8.4.1"),sQuery(id+"F0.wireOp",EDGE,"E8.4.2")])]});
            fillet(context, id + "F6", {"entities" : qUnion([Q0]), "radius" : 0.5 * mm, "tangentPropagation" : true, "allowEdgeOverflow" : false});
        }
        {
            var Q0;
            Q0=makeQuery(id+"F1.opExtrude","CAP_EDGE",EDGE,{"disambiguationData":[OSD([sQuery(id+"F0.wireOp",EDGE,"E0.3")])],"isStart":true});
            var Q1;
            Q1=makeQuery(id+"F1.opExtrude","CAP_EDGE",EDGE,{"disambiguationData":[OSD([sQuery(id+"F0.wireOp",EDGE,"E0.3")])],"isStart":false});
            var Q2;
            Q2=makeQuery(id+"F1.opExtrude","CAP_EDGE",EDGE,{"disambiguationData":[OSD([sQuery(id+"F0.wireOp",EDGE,"E0.2")])],"isStart":false});
            var Q3;
            Q3=makeQuery(id+"F1.opExtrude","CAP_EDGE",EDGE,{"disambiguationData":[OSD([sQuery(id+"F0.wireOp",EDGE,"E0.2")])],"isStart":true});
            var Q4;
            Q4=makeQuery(id+"F1.opExtrude","CAP_EDGE",EDGE,{"disambiguationData":[OSD([sQuery(id+"F0.wireOp",EDGE,"E0.1")])],"isStart":false});
            var Q5;
            Q5=makeQuery(id+"F1.opExtrude","CAP_EDGE",EDGE,{"disambiguationData":[OSD([sQuery(id+"F0.wireOp",EDGE,"E0.1")])],"isStart":true});
            var Q6;
            Q6=makeQuery(id+"F1.opExtrude","SWEPT_EDGE",EDGE,{"disambiguationData":[OSD([sQuery(id+"F0.wireOp",EDGE,"E0.3"),sQuery(id+"F0.wireOp",EDGE,"E8.4.5")])]});
            var Q7;
            Q7=makeQuery(id+"F1.opExtrude","CAP_EDGE",EDGE,{"disambiguationData":[OSD([sQuery(id+"F0.wireOp",EDGE,"E0.4")])],"isStart":false});
            var Q8;
            Q8=makeQuery(id+"F1.opExtrude","CAP_EDGE",EDGE,{"disambiguationData":[OSD([sQuery(id+"F0.wireOp",EDGE,"E0.4")])],"isStart":true});
            var Q9;
            Q9=makeQuery(id+"F1.opExtrude","CAP_EDGE",EDGE,{"disambiguationData":[OSD([sQuery(id+"F0.wireOp",EDGE,"E15.trimOffspring")])],"isStart":true});
            var Q10;
            Q10=makeQuery(id+"F1.opExtrude","CAP_EDGE",EDGE,{"disambiguationData":[OSD([sQuery(id+"F0.wireOp",EDGE,"E15.trimOffspring")])],"isStart":false});
            var Q11;
            Q11=makeQuery(id+"F1.opExtrude","CAP_EDGE",EDGE,{"disambiguationData":[OSD([sQuery(id+"F0.wireOp",EDGE,"E0.0")])],"isStart":false});
            var Q12;
            Q12=makeQuery(id+"F1.opExtrude","CAP_EDGE",EDGE,{"disambiguationData":[OSD([sQuery(id+"F0.wireOp",EDGE,"E22.trimOffspring")])],"isStart":false});
            var Q13;
            Q13=makeQuery(id+"F1.opExtrude","CAP_EDGE",EDGE,{"disambiguationData":[OSD([sQuery(id+"F0.wireOp",EDGE,"E0.0")])],"isStart":true});
            var Q14;
            Q14=makeQuery(id+"F1.opExtrude","CAP_EDGE",EDGE,{"disambiguationData":[OSD([sQuery(id+"F0.wireOp",EDGE,"E22.trimOffspring")])],"isStart":true});
            var Q15;
            Q15=makeQuery(id+"F1.opExtrude","CAP_EDGE",EDGE,{"disambiguationData":[OSD([sQuery(id+"F0.wireOp",EDGE,"E19.trimOffspring")])],"isStart":true});
            var Q16;
            Q16=makeQuery(id+"F1.opExtrude","CAP_EDGE",EDGE,{"disambiguationData":[OSD([sQuery(id+"F0.wireOp",EDGE,"E19.trimOffspring")])],"isStart":false});
            var Q17;
            Q17=makeQuery(id+"F1.opExtrude","CAP_EDGE",EDGE,{"disambiguationData":[OSD([sQuery(id+"F0.wireOp",EDGE,"E24.trimOffspring")])],"isStart":true});
            var Q18;
            Q18=makeQuery(id+"F1.opExtrude","CAP_EDGE",EDGE,{"disambiguationData":[OSD([sQuery(id+"F0.wireOp",EDGE,"E23.trimOffspring")])],"isStart":false});
            var Q19;
            Q19=makeQuery(id+"F1.opExtrude","CAP_EDGE",EDGE,{"disambiguationData":[OSD([sQuery(id+"F0.wireOp",EDGE,"E23.trimOffspring")])],"isStart":true});
            var Q20;
            Q20=makeQuery(id+"F1.opExtrude","CAP_EDGE",EDGE,{"disambiguationData":[OSD([sQuery(id+"F0.wireOp",EDGE,"E0.7")])],"isStart":false});
            var Q21;
            Q21=makeQuery(id+"F1.opExtrude","CAP_EDGE",EDGE,{"disambiguationData":[OSD([sQuery(id+"F0.wireOp",EDGE,"E0.7")])],"isStart":true});
            var Q22;
            Q22=makeQuery(id+"F1.opExtrude","CAP_EDGE",EDGE,{"disambiguationData":[OSD([sQuery(id+"F0.wireOp",EDGE,"E0.8")])],"isStart":true});
            fillet(context, id + "F7", {"entities" : qUnion([Q0, Q1, Q2, Q3, Q4, Q5, Q6, Q7, Q8, Q9, Q10, Q11, Q12, Q13, Q14, Q15, Q16, Q17, Q18, Q19, Q20, Q21, Q22]), "radius" : .5 * mm, "tangentPropagation" : true, "allowEdgeOverflow" : false});
        }
        {
            var Q0;
            Q0=makeQuery(id+"F1.opExtrude","SWEPT_EDGE",EDGE,{"disambiguationData":[OSD([sQuery(id+"F0.wireOp",EDGE,"E0.8"),sQuery(id+"F0.wireOp",EDGE,"E23.trimOffspring")])]});
            var Q1;
            Q1=makeQuery(id+"F1.opExtrude","SWEPT_EDGE",EDGE,{"disambiguationData":[OSD([sQuery(id+"F0.wireOp",EDGE,"E0.0"),sQuery(id+"F0.wireOp",EDGE,"E22.trimOffspring")])]});
            var Q2;
            Q2=makeQuery(id+"F1.opExtrude","SWEPT_EDGE",EDGE,{"disambiguationData":[OSD([sQuery(id+"F0.wireOp",EDGE,"E0.1"),sQuery(id+"F0.wireOp",EDGE,"E15.trimOffspring")])]});
            fillet(context, id + "F8", {"entities" : qUnion([Q0, Q1, Q2]), "radius" : .5 * mm, "tangentPropagation" : true, "allowEdgeOverflow" : false});
        }
        {
            var Q0;
            Q0=makeQuery(id+"F1.opExtrude","CAP_FACE",FACE,{"disambiguationData":[OSD([sQuery(id+"F0.wireOp",EDGE,"E0.0"),sQuery(id+"F0.wireOp",EDGE,"E0.1"),sQuery(id+"F0.wireOp",EDGE,"E0.2"),sQuery(id+"F0.wireOp",EDGE,"E0.3"),sQuery(id+"F0.wireOp",EDGE,"E0.4"),sQuery(id+"F0.wireOp",EDGE,"E0.5"),sQuery(id+"F0.wireOp",EDGE,"E0.6"),sQuery(id+"F0.wireOp",EDGE,"E0.7"),sQuery(id+"F0.wireOp",EDGE,"E0.8"),sQuery(id+"F0.wireOp",EDGE,"E1"),sQuery(id+"F0.wireOp",EDGE,"E2"),sQuery(id+"F0.wireOp",EDGE,"E3"),sQuery(id+"F0.wireOp",EDGE,"E4"),sQuery(id+"F0.wireOp",EDGE,"E5"),sQuery(id+"F0.wireOp",EDGE,"E6"),sQuery(id+"F0.wireOp",EDGE,"E7"),sQuery(id+"F0.wireOp",EDGE,"E8.1.0"),sQuery(id+"F0.wireOp",EDGE,"E8.1.1"),sQuery(id+"F0.wireOp",EDGE,"E8.1.2"),sQuery(id+"F0.wireOp",EDGE,"E8.1.3"),sQuery(id+"F0.wireOp",EDGE,"E8.1.4"),sQuery(id+"F0.wireOp",EDGE,"E8.1.5"),sQuery(id+"F0.wireOp",EDGE,"E8.1.6"),sQuery(id+"F0.wireOp",EDGE,"E8.2.0"),sQuery(id+"F0.wireOp",EDGE,"E8.2.1"),sQuery(id+"F0.wireOp",EDGE,"E8.2.2"),sQuery(id+"F0.wireOp",EDGE,"E8.2.3"),sQuery(id+"F0.wireOp",EDGE,"E8.2.4"),sQuery(id+"F0.wireOp",EDGE,"E8.2.5"),sQuery(id+"F0.wireOp",EDGE,"E8.2.6"),sQuery(id+"F0.wireOp",EDGE,"E8.3.0"),sQuery(id+"F0.wireOp",EDGE,"E8.3.1"),sQuery(id+"F0.wireOp",EDGE,"E8.3.2"),sQuery(id+"F0.wireOp",EDGE,"E8.3.3"),sQuery(id+"F0.wireOp",EDGE,"E8.3.4"),sQuery(id+"F0.wireOp",EDGE,"E8.3.5"),sQuery(id+"F0.wireOp",EDGE,"E8.3.6"),sQuery(id+"F0.wireOp",EDGE,"E8.4.0"),sQuery(id+"F0.wireOp",EDGE,"E8.4.1"),sQuery(id+"F0.wireOp",EDGE,"E8.4.2"),sQuery(id+"F0.wireOp",EDGE,"E8.4.3"),sQuery(id+"F0.wireOp",EDGE,"E8.4.4"),sQuery(id+"F0.wireOp",EDGE,"E8.4.5"),sQuery(id+"F0.wireOp",EDGE,"E8.4.6"),sQuery(id+"F0.wireOp",EDGE,"E8.5.0"),sQuery(id+"F0.wireOp",EDGE,"E8.5.1"),sQuery(id+"F0.wireOp",EDGE,"E8.5.2"),sQuery(id+"F0.wireOp",EDGE,"E8.5.3"),sQuery(id+"F0.wireOp",EDGE,"E8.5.4"),sQuery(id+"F0.wireOp",EDGE,"E8.5.5"),sQuery(id+"F0.wireOp",EDGE,"E8.5.6"),sQuery(id+"F0.wireOp",EDGE,"E8.6.0"),sQuery(id+"F0.wireOp",EDGE,"E8.6.1"),sQuery(id+"F0.wireOp",EDGE,"E8.6.2"),sQuery(id+"F0.wireOp",EDGE,"E8.6.3"),sQuery(id+"F0.wireOp",EDGE,"E8.6.4"),sQuery(id+"F0.wireOp",EDGE,"E8.6.5"),sQuery(id+"F0.wireOp",EDGE,"E8.6.6"),sQuery(id+"F0.wireOp",EDGE,"E8.7.0"),sQuery(id+"F0.wireOp",EDGE,"E8.7.1"),sQuery(id+"F0.wireOp",EDGE,"E8.7.2"),sQuery(id+"F0.wireOp",EDGE,"E8.7.3"),sQuery(id+"F0.wireOp",EDGE,"E8.7.4"),sQuery(id+"F0.wireOp",EDGE,"E8.7.5"),sQuery(id+"F0.wireOp",EDGE,"E8.7.6"),sQuery(id+"F0.wireOp",EDGE,"E9"),sQuery(id+"F0.wireOp",EDGE,"E10"),sQuery(id+"F0.wireOp",EDGE,"E11"),sQuery(id+"F0.wireOp",EDGE,"E13.trimOffspring"),sQuery(id+"F0.wireOp",EDGE,"E15.trimOffspring"),sQuery(id+"F0.wireOp",EDGE,"E19.trimOffspring"),sQuery(id+"F0.wireOp",EDGE,"E22.trimOffspring"),sQuery(id+"F0.wireOp",EDGE,"E23.trimOffspring"),sQuery(id+"F0.wireOp",EDGE,"E24.trimOffspring")])],"isStart":false});
            var sketch = newSketch(context, id + "F9", { "sketchPlane" : qUnion([Q0])});
            skText(sketch, "E25", { "text": "Yael\nC. S.", "fontName": "OpenSans-Bold.ttf"});
            const initialGuessF9  = {"E25": [-0.00612, 0.00151, 1, 0, 0.00453]};
            skSetInitialGuess(sketch, initialGuessF9);
            skSolve(sketch);
        }
        {
            var Q0;
            Q0 = qSketchRegion(id + "F9", true);
            extrude(context, id + "F10", {"entities" : qUnion([Q0]), "operationType" : NewBodyOperationType.ADD, "depth" : 1 * mm, "offsetDistance" : 25 * mm});
        }
    });
